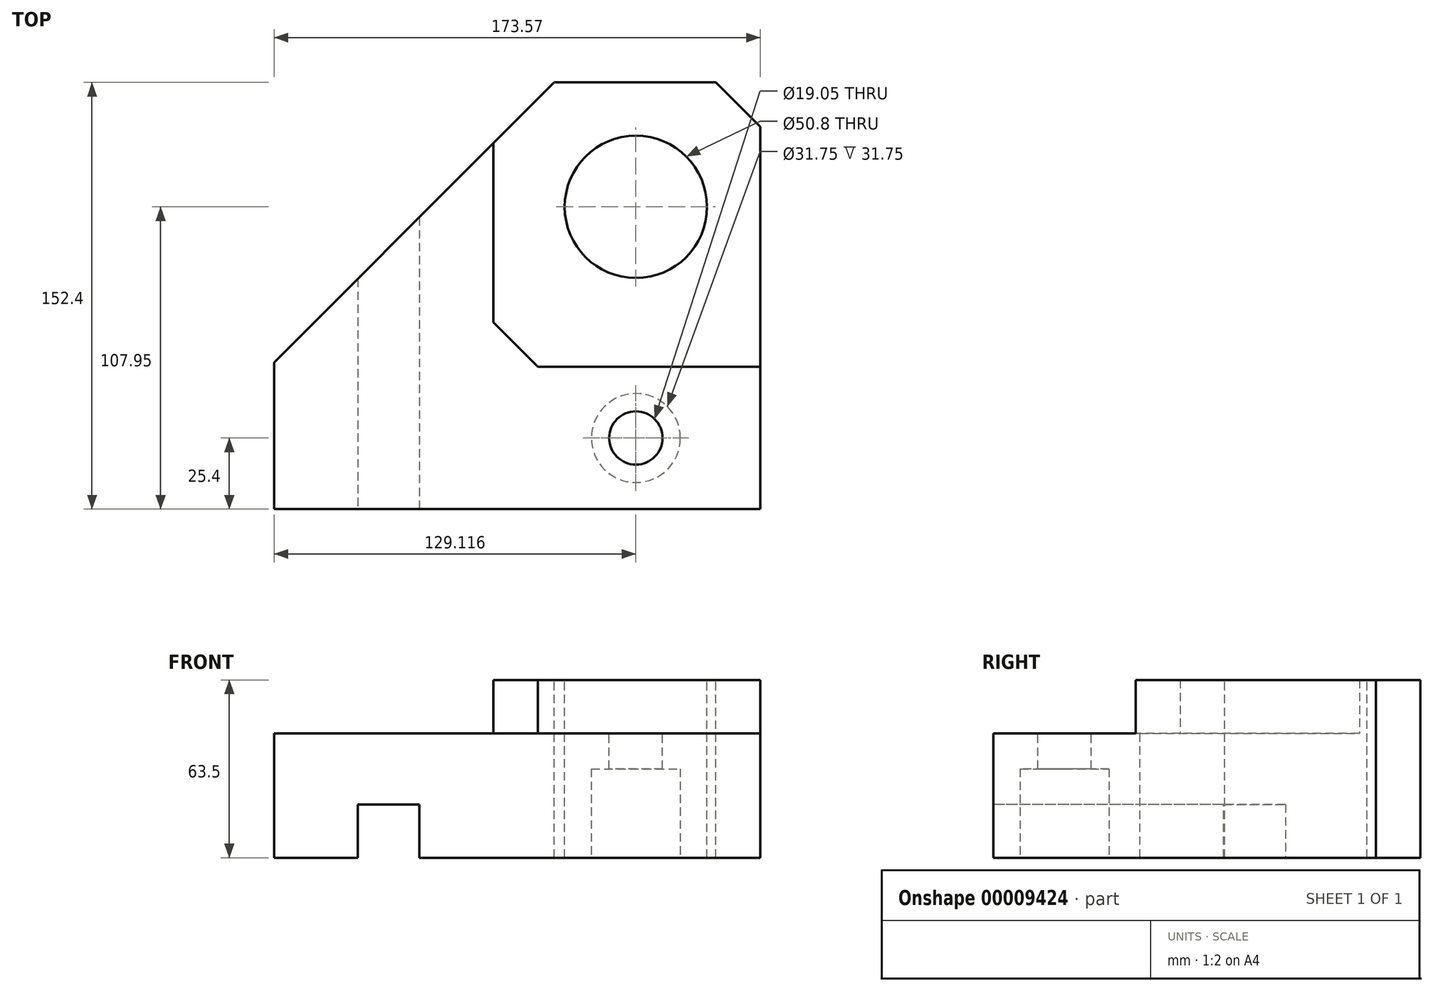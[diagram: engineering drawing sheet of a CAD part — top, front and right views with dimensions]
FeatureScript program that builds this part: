
annotation { "Feature Type Name" : "Feature", "Feature Type Description" : "" }
export const myFeature = defineFeature(function(context is Context, id is Id, definition is map)
    precondition{}
    {
        {
            var Q0;
            Q0=qCreatedBy(makeId("Top.planeOp"),FACE);
            var sketch = newSketch(context, id + "F0", { "sketchPlane" : qUnion([Q0])});
            skLineSegment(sketch, "E0", {"start": v(73.36, 66.3) * mm, "end": v(73.36, -70.23) * mm});
            skLineSegment(sketch, "E1", {"start": v(73.36, -70.23) * mm, "end": v(-100.21, -70.23) * mm});
            skLineSegment(sketch, "E2", {"start": v(-100.21, -70.23) * mm, "end": v(-100.21, -17.84) * mm});
            skLineSegment(sketch, "E3", {"start": v(-100.21, -17.84) * mm, "end": v(-0.2, 82.17) * mm});
            skLineSegment(sketch, "E4", {"start": v(-0.2, 82.17) * mm, "end": v(57.48, 82.17) * mm});
            skLineSegment(sketch, "E5", {"start": v(-21.9, 60.47) * mm, "end": v(-21.9, -3.55) * mm});
            skLineSegment(sketch, "E6", {"start": v(-21.9, -3.55) * mm, "end": v(-6.02, -19.43) * mm});
            skLineSegment(sketch, "E7", {"start": v(-6.02, -19.43) * mm, "end": v(73.36, -19.43) * mm});
            skLineSegment(sketch, "E8", {"start": v(73.36, 66.3) * mm, "end": v(57.48, 82.17) * mm});
            skCircle(sketch, "E9", {"center": v(28.9, 37.72) * mm, "radius": 25.4 * mm});
            skCircle(sketch, "E10", {"center": v(28.9, -44.83) * mm, "radius": 9.53 * mm});
            skCircle(sketch, "E11", {"center": v(28.9, -44.83) * mm, "radius": 15.88 * mm});
            skLineSegment(sketch, "E12", {"start": v(-71.64, -70.23) * mm, "end": v(-71.64, 10.73) * mm});
            skLineSegment(sketch, "E13", {"start": v(-47.82, -70.23) * mm, "end": v(-47.82, 34.55) * mm});
            skPoint(sketch, "E14.orphan", {"position": v(73.36, 82.17) * mm});
            skSolve(sketch);
        }
        {
            var Q0;
            {var subQ3=sQuery(id+"F0.wireOp",EDGE,"E4");Q0=makeQuery(id+"F0.imprint","IMPRINT",FACE,{"disambiguationData":[TD([[makeQuery(id+"F0.imprint","IMPRINT",EDGE,{"derivedFrom":subQ3}),-1.0]])]});}
            var Q1;
            {var subQ2=sQuery(id+"F0.wireOp",EDGE,"E5");Q1=makeQuery(id+"F0.imprint","IMPRINT",FACE,{"disambiguationData":[TD([[makeQuery(id+"F0.imprint","IMPRINT",EDGE,{"derivedFrom":subQ2}),-1.0]])]});}
            var Q2;
            {var subQ0=sQuery(id+"F0.wireOp",EDGE,"E12");Q2=makeQuery(id+"F0.imprint","IMPRINT",FACE,{"disambiguationData":[TD([[makeQuery(id+"F0.imprint","IMPRINT",EDGE,{"derivedFrom":subQ0}),-1.0]])]});}
            var Q3;
            {var subQ2=sQuery(id+"F0.wireOp",EDGE,"E2");Q3=makeQuery(id+"F0.imprint","IMPRINT",FACE,{"disambiguationData":[TD([[makeQuery(id+"F0.imprint","IMPRINT",EDGE,{"derivedFrom":subQ2}),-1.0]])]});}
            var Q4;
            Q4=makeQuery(id+"F0.imprint","IMPRINT",FACE,{"disambiguationData":[TD([[makeQuery(id+"F0.imprint","IMPRINT",EDGE,{"derivedFrom":sQuery(id+"F0.wireOp",EDGE,"E10")}),-1.0]])]});
            extrude(context, id + "F1", {"entities" : qUnion([Q0, Q1, Q2, Q3, Q4]), "oppositeDirection" : true, "depth" : 44.45 * mm});
        }
        {
            var Q0;
            {var subQ3=sQuery(id+"F0.wireOp",EDGE,"E4");Q0=makeQuery(id+"F0.imprint","IMPRINT",FACE,{"disambiguationData":[TD([[makeQuery(id+"F0.imprint","IMPRINT",EDGE,{"derivedFrom":subQ3}),-1.0]])]});}
            extrude(context, id + "F2", {"entities" : qUnion([Q0]), "operationType" : NewBodyOperationType.ADD, "depth" : 19.05 * mm});
        }
        {
            var Q0;
            Q0=makeQuery(id+"F1.opExtrude","CAP_FACE",FACE,{"disambiguationData":[OSD([sQuery(id+"F0.wireOp",EDGE,"E0"),sQuery(id+"F0.wireOp",EDGE,"E1"),sQuery(id+"F0.wireOp",EDGE,"E2"),sQuery(id+"F0.wireOp",EDGE,"E3"),sQuery(id+"F0.wireOp",EDGE,"E4"),sQuery(id+"F0.wireOp",EDGE,"E8"),sQuery(id+"F0.wireOp",EDGE,"E9"),sQuery(id+"F0.wireOp",EDGE,"E10")])],"isStart":false});
            var sketch = newSketch(context, id + "F3", { "sketchPlane" : qUnion([Q0])});
            skCircle(sketch, "E15", {"center": v(28.9, 44.83) * mm, "radius": 15.88 * mm});
            skSolve(sketch);
        }
        {
            var Q0;
            Q0=makeQuery(id+"F3.imprint","IMPRINT",FACE,{"disambiguationData":[TD([[makeQuery(id+"F3.imprint","IMPRINT",EDGE,{"derivedFrom":sQuery(id+"F3.wireOp",EDGE,"E15")}),1.0]])]});
            extrude(context, id + "F4", {"entities" : qUnion([Q0]), "operationType" : NewBodyOperationType.REMOVE, "oppositeDirection" : true, "depth" : 31.75 * mm});
        }
        {
            var Q0;
            Q0=makeQuery(id+"F1.opExtrude","SWEPT_FACE",FACE,{"disambiguationData":[OSD([sQuery(id+"F0.wireOp",EDGE,"E1")])]});
            var sketch = newSketch(context, id + "F5", { "sketchPlane" : qUnion([Q0])});
            skLineSegment(sketch, "E16", {"start": v(-70.34, 0) * mm, "end": v(-70.34, -44.45) * mm, "construction": true});
            skLineSegment(sketch, "E17", {"start": v(-48.33, 0) * mm, "end": v(-48.33, -44.45) * mm, "construction": true});
            skLineSegment(sketch, "E18", {"start": v(-70.34, -44.45) * mm, "end": v(-70.34, -25.4) * mm});
            skLineSegment(sketch, "E19", {"start": v(-70.34, -25.4) * mm, "end": v(-48.33, -25.4) * mm});
            skLineSegment(sketch, "E20", {"start": v(-48.33, -25.4) * mm, "end": v(-48.33, -44.45) * mm});
            skSolve(sketch);
        }
        {
            var Q0;
            {var subQ2=sQuery(id+"F5.wireOp",EDGE,"E18");Q0=makeQuery(id+"F5.imprint","IMPRINT",FACE,{"disambiguationData":[TD([[makeQuery(id+"F5.imprint","IMPRINT",EDGE,{"derivedFrom":subQ2}),-1.0]])]});}
            extrude(context, id + "F6", {"entities" : qUnion([Q0]), "operationType" : NewBodyOperationType.REMOVE, "endBound" : BoundingType.THROUGH_ALL, "oppositeDirection" : true, "depth" : 25.4 * mm});
        }
    });
